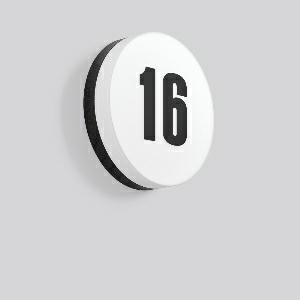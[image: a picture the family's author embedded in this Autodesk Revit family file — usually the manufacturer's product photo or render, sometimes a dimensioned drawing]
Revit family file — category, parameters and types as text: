
# Revit family: flat_slim_round_312630_0031_25_44c2
name_source: partatom
category: Lighting Fixtures
units: mm (PartAtom-declared; Revit-internal decimal feet)

## family parameters
Cut with Voids When Loaded = No
Host = Face
Light Source = No
Part Type = Normal
Room Calculation Point = No
Round Connector Dimension = Use Diameter
Shared = No

## types (1)
- MultiLumen 1 830 (1 x LED Modul 830, 1300 lm, 3000)
    Apparent Load = 11 VA
    CIE Flux Codes = 39 70 89 83 100
    Color Rendering = 80
    Color Temperature = 3000
    Default Elevation = 1800 mm
    Height = 70 mm
    Lamp = 1 x LED Modul 830
    Lamp Light Flux = 1300 lm
    Lamp count = 1
    Length = 300 mm
    Lifetime = 50000 h
    Luminous efficacy = 118 lm/W
    Manufacturer = RZB
    ModVariant = No
    Model = 312630.0031.25
    Mounting Place = Wall
    Mounting Type = Surface mounted
    Number of Poles = 1
    OnlyDefault = Yes
    Power Factor = 1
    Product Name = FLAT SLIM round
    Product group = Hous number luminaires
    ProductGroupID = 2003
    Protection Class = Protection class I
    Protection Degree = Degree of protection
    RLX_Detail_Level = 1
    RLX_Emergency_Light_Flux = 0 lm
    RLX_Emergency_Type = 0
    RLX_Emergency_Type_DB = No
    RlxData = <blob elided: 31057 chars, md5=ca6d9a97>
    Socket = socket
    Standby Power = 0 W
    System Light Flux = 1300 lm
    System Power = 11 W
    Type Comments = MultiLumen 1 830
    Type Image = 312629.0031_hn16.jpg
    URL = http://relux.com
    VarID = multilumen_1_830
    Voltage = 0 V
    Weight = 0.00 kg
    Width = 0 mm  [stored 0 ft]

note: [stored X ft] marks values corroborated as IEEE doubles in the binary element streams (Revit-internal decimal feet)

## geometry (parser evidence)
native form markers: Blend x4, Sweep x13
no freeform markers — native parametric forms only
